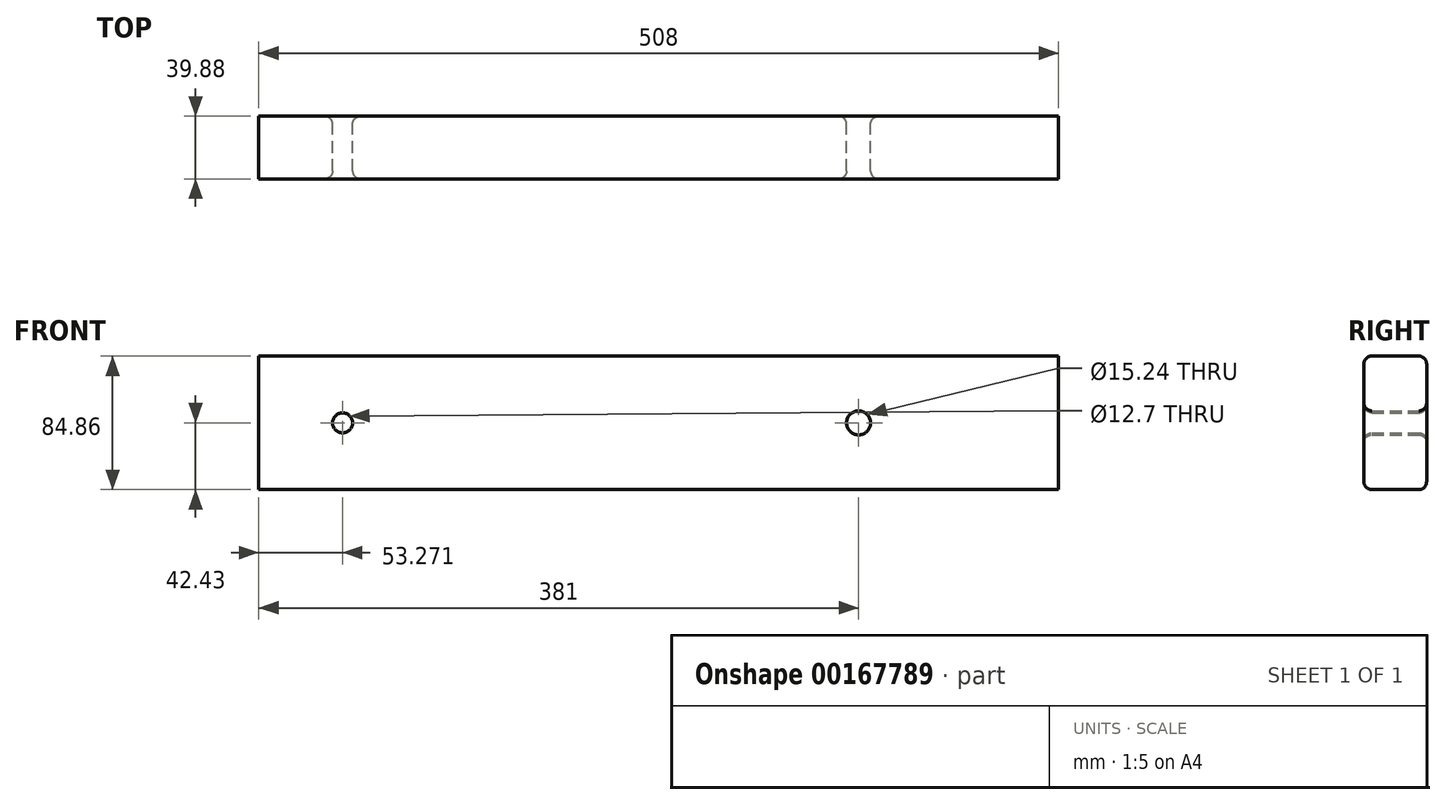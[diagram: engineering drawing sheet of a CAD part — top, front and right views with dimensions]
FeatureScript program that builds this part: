
annotation { "Feature Type Name" : "Feature", "Feature Type Description" : "" }
export const myFeature = defineFeature(function(context is Context, id is Id, definition is map)
    precondition{}
    {
        {
            var Q0;
            Q0=qCreatedBy(makeId("Front.planeOp"),FACE);
            var sketch = newSketch(context, id + "F0", { "sketchPlane" : qUnion([Q0])});
            skLineSegment(sketch, "E0.bottom", {"start": v(254, -42.43) * mm, "end": v(-254, -42.43) * mm});
            skLineSegment(sketch, "E0.top", {"start": v(254, 42.43) * mm, "end": v(-254, 42.43) * mm});
            skLineSegment(sketch, "E0.left", {"start": v(254, -42.43) * mm, "end": v(254, 42.43) * mm});
            skLineSegment(sketch, "E0.right", {"start": v(-254, -42.43) * mm, "end": v(-254, 42.43) * mm});
            skPoint(sketch, "E0.middle", {"position": v(0, 0) * mm});
            skLineSegment(sketch, "E1", {"start": v(254, 42.43) * mm, "end": v(127, 42.43) * mm});
            skCircle(sketch, "E2", {"center": v(127, 0) * mm, "radius": 7.62 * mm});
            skLineSegment(sketch, "E3", {"start": v(-254, 42.43) * mm, "end": v(-200.73, 42.43) * mm});
            skCircle(sketch, "E4", {"center": v(-200.73, 0) * mm, "radius": 6.35 * mm});
            skSolve(sketch);
        }
        {
            var Q0;
            Q0=qSketchRegion(id+"F0",true);
            extrude(context, id + "F1", {"entities" : qUnion([Q0]), "depth" : 39.88 * mm});
        }
        {
            var Q0;
            Q0=makeQuery(id+"F1.opExtrude","CAP_EDGE",EDGE,{"disambiguationData":[OSD([sQuery(id+"F0.wireOp",EDGE,"E0.top"),sQuery(id+"F0.wireOp",EDGE,"E1"),sQuery(id+"F0.wireOp",EDGE,"E3")])],"isStart":true});
            var Q1;
            Q1=makeQuery(id+"F1.opExtrude","CAP_EDGE",EDGE,{"disambiguationData":[OSD([sQuery(id+"F0.wireOp",EDGE,"E0.bottom")])],"isStart":true});
            var Q2;
            Q2=makeQuery(id+"F1.opExtrude","CAP_EDGE",EDGE,{"disambiguationData":[OSD([sQuery(id+"F0.wireOp",EDGE,"E2")])],"isStart":true});
            var Q3;
            Q3=makeQuery(id+"F1.opExtrude","CAP_EDGE",EDGE,{"disambiguationData":[OSD([sQuery(id+"F0.wireOp",EDGE,"E4")])],"isStart":true});
            var Q4;
            Q4=makeQuery(id+"F1.opExtrude","CAP_EDGE",EDGE,{"disambiguationData":[OSD([sQuery(id+"F0.wireOp",EDGE,"E0.top"),sQuery(id+"F0.wireOp",EDGE,"E1"),sQuery(id+"F0.wireOp",EDGE,"E3")])],"isStart":false});
            var Q5;
            Q5=makeQuery(id+"F1.opExtrude","CAP_EDGE",EDGE,{"disambiguationData":[OSD([sQuery(id+"F0.wireOp",EDGE,"E0.bottom")])],"isStart":false});
            var Q6;
            Q6=makeQuery(id+"F1.opExtrude","CAP_EDGE",EDGE,{"disambiguationData":[OSD([sQuery(id+"F0.wireOp",EDGE,"E4")])],"isStart":false});
            var Q7;
            Q7=makeQuery(id+"F1.opExtrude","CAP_EDGE",EDGE,{"disambiguationData":[OSD([sQuery(id+"F0.wireOp",EDGE,"E2")])],"isStart":false});
            fillet(context, id + "F2", {"entities" : qUnion([Q0, Q1, Q2, Q3, Q4, Q5, Q6, Q7]), "radius" : 5.08 * mm, "tangentPropagation" : true, "allowEdgeOverflow" : false});
        }
    });
